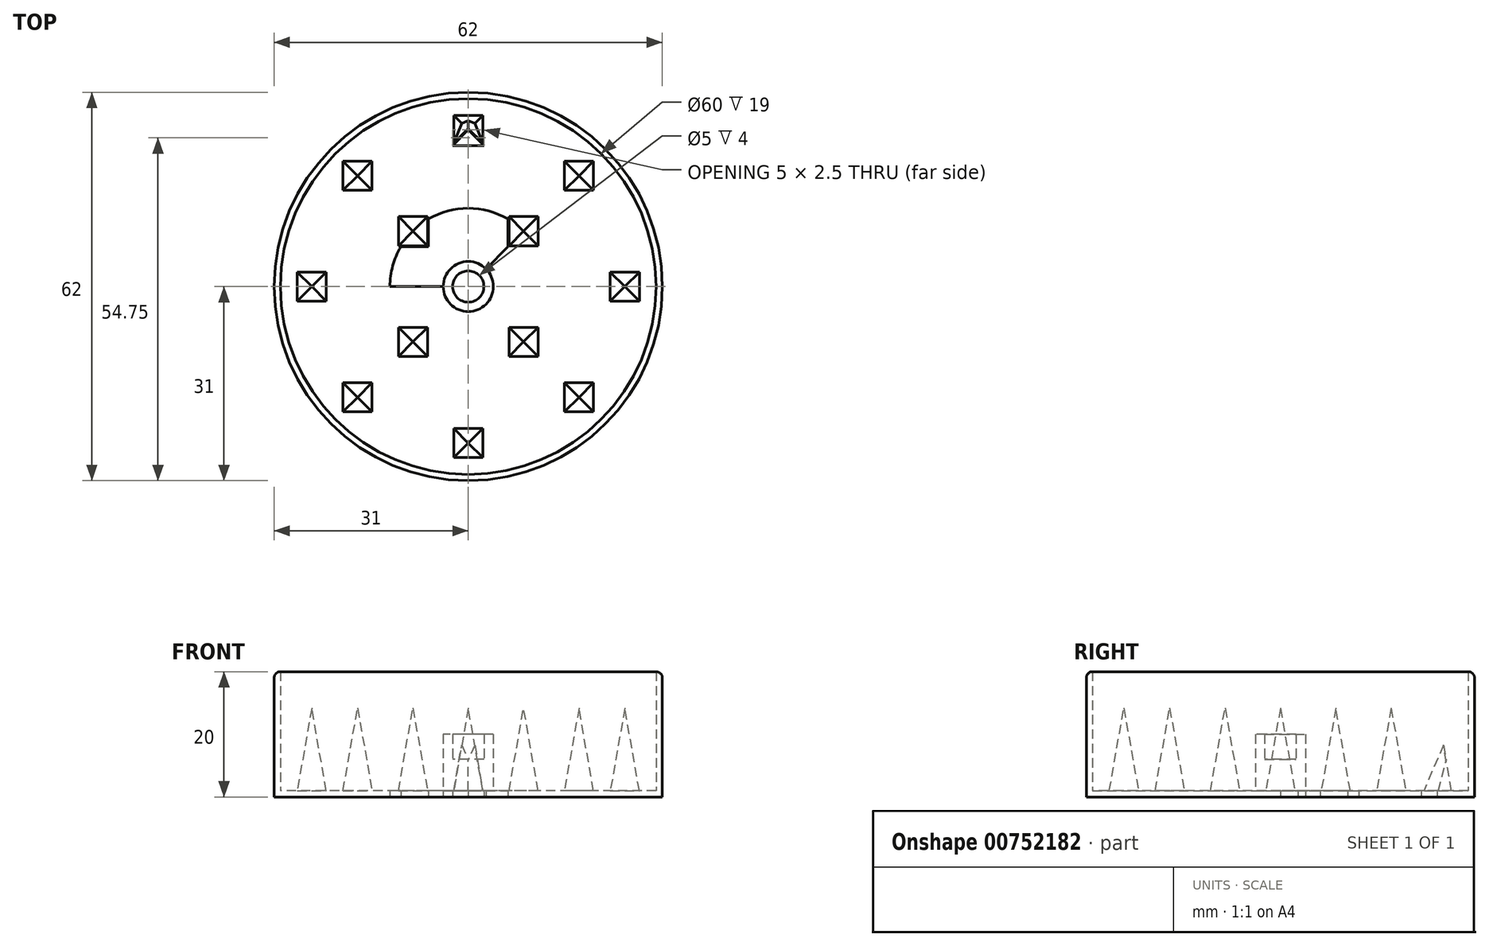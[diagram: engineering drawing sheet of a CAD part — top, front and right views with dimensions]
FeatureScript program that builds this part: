
annotation { "Feature Type Name" : "Feature", "Feature Type Description" : "" }
export const myFeature = defineFeature(function(context is Context, id is Id, definition is map)
    precondition{}
    {
        {
            var Q0;
            Q0=qCreatedBy(makeId("Top.planeOp"),FACE);
            var sketch = newSketch(context, id + "F0", { "sketchPlane" : qUnion([Q0])});
            skCircle(sketch, "E0", {"center": v(0, 0) * mm, "radius": 30 * mm});
            skCircle(sketch, "E1", {"center": v(0, 0) * mm, "radius": 31 * mm});
            skLineSegment(sketch, "E2", {"start": v(0, 0) * mm, "end": v(0, 25) * mm});
            skLineSegment(sketch, "E3", {"start": v(0, 25) * mm, "end": v(0, 0) * mm});
            skLineSegment(sketch, "E4", {"start": v(0, -25) * mm, "end": v(0, 0) * mm});
            skLineSegment(sketch, "E5", {"start": v(0, 0) * mm, "end": v(25, 0) * mm});
            skLineSegment(sketch, "E6", {"start": v(0, 0) * mm, "end": v(-25, 0) * mm});
            skLineSegment(sketch, "E7.bottom", {"start": v(-22.5, -2.5) * mm, "end": v(-27.5, -2.5) * mm});
            skLineSegment(sketch, "E7.top", {"start": v(-22.5, 2.5) * mm, "end": v(-27.5, 2.5) * mm});
            skLineSegment(sketch, "E7.left", {"start": v(-22.5, -2.5) * mm, "end": v(-22.5, 2.5) * mm});
            skLineSegment(sketch, "E7.right", {"start": v(-27.5, -2.5) * mm, "end": v(-27.5, 2.5) * mm});
            skPoint(sketch, "E7.middle", {"position": v(-25, 0) * mm});
            skLineSegment(sketch, "E8.bottom", {"start": v(2.5, 22.5) * mm, "end": v(-2.5, 22.5) * mm});
            skLineSegment(sketch, "E8.top", {"start": v(2.5, 27.5) * mm, "end": v(-2.5, 27.5) * mm});
            skLineSegment(sketch, "E8.left", {"start": v(2.5, 22.5) * mm, "end": v(2.5, 27.5) * mm});
            skLineSegment(sketch, "E8.right", {"start": v(-2.5, 22.5) * mm, "end": v(-2.5, 27.5) * mm});
            skPoint(sketch, "E8.middle", {"position": v(0, 25) * mm});
            skLineSegment(sketch, "E9.bottom", {"start": v(27.5, -2.5) * mm, "end": v(22.5, -2.5) * mm});
            skLineSegment(sketch, "E9.top", {"start": v(27.5, 2.5) * mm, "end": v(22.5, 2.5) * mm});
            skLineSegment(sketch, "E9.left", {"start": v(27.5, -2.5) * mm, "end": v(27.5, 2.5) * mm});
            skLineSegment(sketch, "E9.right", {"start": v(22.5, -2.5) * mm, "end": v(22.5, 2.5) * mm});
            skPoint(sketch, "E9.middle", {"position": v(25, 0) * mm});
            skLineSegment(sketch, "E10.bottom", {"start": v(2.5, -22.5) * mm, "end": v(-2.5, -22.5) * mm});
            skLineSegment(sketch, "E10.top", {"start": v(2.5, -27.5) * mm, "end": v(-2.5, -27.5) * mm});
            skLineSegment(sketch, "E10.left", {"start": v(2.5, -22.5) * mm, "end": v(2.5, -27.5) * mm});
            skLineSegment(sketch, "E10.right", {"start": v(-2.5, -22.5) * mm, "end": v(-2.5, -27.5) * mm});
            skPoint(sketch, "E10.middle", {"position": v(0, -25) * mm});
            skLineSegment(sketch, "E11", {"start": v(0, 0) * mm, "end": v(17.68, 17.68) * mm});
            skLineSegment(sketch, "E12.bottom", {"start": v(20.18, 15.18) * mm, "end": v(15.18, 15.18) * mm});
            skLineSegment(sketch, "E12.top", {"start": v(20.18, 20.18) * mm, "end": v(15.18, 20.18) * mm});
            skLineSegment(sketch, "E12.left", {"start": v(20.18, 15.18) * mm, "end": v(20.18, 20.18) * mm});
            skLineSegment(sketch, "E12.right", {"start": v(15.18, 15.18) * mm, "end": v(15.18, 20.18) * mm});
            skPoint(sketch, "E12.middle", {"position": v(17.68, 17.68) * mm});
            skLineSegment(sketch, "E13.1.0", {"start": v(-20.18, 20.18) * mm, "end": v(-20.18, 15.18) * mm});
            skLineSegment(sketch, "E13.1.1", {"start": v(-15.18, 20.18) * mm, "end": v(-20.18, 20.18) * mm});
            skLineSegment(sketch, "E13.1.2", {"start": v(-15.18, 20.18) * mm, "end": v(-15.18, 15.18) * mm});
            skLineSegment(sketch, "E13.1.3", {"start": v(-15.18, 15.18) * mm, "end": v(-20.18, 15.18) * mm});
            skLineSegment(sketch, "E13.2.0", {"start": v(-20.18, -20.18) * mm, "end": v(-15.18, -20.18) * mm});
            skLineSegment(sketch, "E13.2.1", {"start": v(-20.18, -15.18) * mm, "end": v(-20.18, -20.18) * mm});
            skLineSegment(sketch, "E13.2.2", {"start": v(-20.18, -15.18) * mm, "end": v(-15.18, -15.18) * mm});
            skLineSegment(sketch, "E13.2.3", {"start": v(-15.18, -15.18) * mm, "end": v(-15.18, -20.18) * mm});
            skLineSegment(sketch, "E13.3.0", {"start": v(20.18, -20.18) * mm, "end": v(20.18, -15.18) * mm});
            skLineSegment(sketch, "E13.3.1", {"start": v(15.18, -20.18) * mm, "end": v(20.18, -20.18) * mm});
            skLineSegment(sketch, "E13.3.2", {"start": v(15.18, -20.18) * mm, "end": v(15.18, -15.18) * mm});
            skLineSegment(sketch, "E13.3.3", {"start": v(15.18, -15.18) * mm, "end": v(20.18, -15.18) * mm});
            skPoint(sketch, "E14", {"position": v(8.84, 8.84) * mm});
            skLineSegment(sketch, "E15.bottom", {"start": v(11.34, 6.34) * mm, "end": v(6.34, 6.34) * mm});
            skLineSegment(sketch, "E15.top", {"start": v(11.34, 11.34) * mm, "end": v(6.34, 11.34) * mm});
            skLineSegment(sketch, "E15.left", {"start": v(11.34, 6.34) * mm, "end": v(11.34, 11.34) * mm});
            skLineSegment(sketch, "E15.right", {"start": v(6.34, 6.34) * mm, "end": v(6.34, 11.34) * mm});
            skLineSegment(sketch, "E16.1.0", {"start": v(-11.34, 11.34) * mm, "end": v(-11.34, 6.34) * mm});
            skLineSegment(sketch, "E16.1.1", {"start": v(-6.34, 11.34) * mm, "end": v(-11.34, 11.34) * mm});
            skLineSegment(sketch, "E16.1.2", {"start": v(-6.34, 11.34) * mm, "end": v(-6.34, 6.34) * mm});
            skLineSegment(sketch, "E16.1.3", {"start": v(-6.34, 6.34) * mm, "end": v(-11.34, 6.34) * mm});
            skLineSegment(sketch, "E16.2.0", {"start": v(-11.34, -11.34) * mm, "end": v(-6.34, -11.34) * mm});
            skLineSegment(sketch, "E16.2.1", {"start": v(-11.34, -6.34) * mm, "end": v(-11.34, -11.34) * mm});
            skLineSegment(sketch, "E16.2.2", {"start": v(-11.34, -6.34) * mm, "end": v(-6.34, -6.34) * mm});
            skLineSegment(sketch, "E16.2.3", {"start": v(-6.34, -6.34) * mm, "end": v(-6.34, -11.34) * mm});
            skLineSegment(sketch, "E16.3.0", {"start": v(11.34, -11.34) * mm, "end": v(11.34, -6.34) * mm});
            skLineSegment(sketch, "E16.3.1", {"start": v(6.34, -11.34) * mm, "end": v(11.34, -11.34) * mm});
            skLineSegment(sketch, "E16.3.2", {"start": v(6.34, -11.34) * mm, "end": v(6.34, -6.34) * mm});
            skLineSegment(sketch, "E16.3.3", {"start": v(6.34, -6.34) * mm, "end": v(11.34, -6.34) * mm});
            skCircle(sketch, "E17", {"center": v(0, 0) * mm, "radius": 4 * mm});
            skLineSegment(sketch, "E18", {"start": v(-20.18, 20.18) * mm, "end": v(-15.18, 15.18) * mm});
            skLineSegment(sketch, "E19", {"start": v(-2.5, 27.5) * mm, "end": v(2.5, 22.5) * mm});
            skLineSegment(sketch, "E20", {"start": v(15.18, 20.18) * mm, "end": v(20.18, 15.18) * mm});
            skLineSegment(sketch, "E21", {"start": v(22.5, 2.5) * mm, "end": v(27.5, -2.5) * mm});
            skLineSegment(sketch, "E22", {"start": v(-11.34, 11.34) * mm, "end": v(-6.34, 6.34) * mm});
            skLineSegment(sketch, "E23", {"start": v(6.34, -6.34) * mm, "end": v(11.34, -11.34) * mm});
            skLineSegment(sketch, "E24", {"start": v(15.18, -15.18) * mm, "end": v(20.18, -20.18) * mm});
            skLineSegment(sketch, "E25", {"start": v(-11.34, -6.34) * mm, "end": v(-6.34, -11.34) * mm});
            skLineSegment(sketch, "E26", {"start": v(-2.5, -22.5) * mm, "end": v(2.5, -27.5) * mm});
            skLineSegment(sketch, "E27", {"start": v(-20.18, -15.18) * mm, "end": v(-15.18, -20.18) * mm});
            skLineSegment(sketch, "E28", {"start": v(2.5, 27.5) * mm, "end": v(-2.5, 22.5) * mm});
            skLineSegment(sketch, "E29", {"start": v(-15.18, 20.18) * mm, "end": v(-20.18, 15.18) * mm});
            skLineSegment(sketch, "E30", {"start": v(-22.5, 2.5) * mm, "end": v(-27.5, -2.5) * mm});
            skLineSegment(sketch, "E31", {"start": v(-27.5, 2.5) * mm, "end": v(-22.5, -2.5) * mm});
            skLineSegment(sketch, "E32", {"start": v(-6.34, 11.34) * mm, "end": v(-11.34, 6.34) * mm});
            skLineSegment(sketch, "E33", {"start": v(6.34, 11.34) * mm, "end": v(11.34, 6.34) * mm});
            skLineSegment(sketch, "E34", {"start": v(20.18, 20.18) * mm, "end": v(17.68, 17.68) * mm});
            skLineSegment(sketch, "E35", {"start": v(27.5, 2.5) * mm, "end": v(22.5, -2.5) * mm});
            skLineSegment(sketch, "E36", {"start": v(20.18, -15.18) * mm, "end": v(15.18, -20.18) * mm});
            skLineSegment(sketch, "E37", {"start": v(11.34, -6.34) * mm, "end": v(6.34, -11.34) * mm});
            skLineSegment(sketch, "E38", {"start": v(-6.34, -6.34) * mm, "end": v(-11.34, -11.34) * mm});
            skLineSegment(sketch, "E39", {"start": v(-15.18, -15.18) * mm, "end": v(-20.18, -20.18) * mm});
            skLineSegment(sketch, "E40", {"start": v(2.5, -22.5) * mm, "end": v(-2.5, -27.5) * mm});
            skCircle(sketch, "E41", {"center": v(0, 0) * mm, "radius": 12.5 * mm});
            skCircle(sketch, "E42", {"center": v(0, 0) * mm, "radius": 21.46 * mm});
            skCircle(sketch, "E43", {"center": v(0, 0) * mm, "radius": 2.5 * mm});
            skSolve(sketch);
        }
        {
            var Q0;
            Q0 = qSketchRegion(id + "F0", true);
            var Q1;
            Q1=makeQuery(id+"F0.imprint","IMPRINT",FACE,{"disambiguationData":[TD([[makeQuery(id+"F0.imprint","IMPRINT",EDGE,{"derivedFrom":sQuery(id+"F0.wireOp",EDGE,"E0")}),1.0]])]});
            var Q2;
            {var subQ1=sQuery(id+"F0.wireOp",EDGE,"E15.top");Q2=makeQuery(id+"F0.imprint","IMPRINT",FACE,{"disambiguationData":[TD([[makeQuery(id+"F0.imprint","IMPRINT",EDGE,{"derivedFrom":subQ1}),-1.0]])]});}
            var Q3;
            {var subQ0=sQuery(id+"F0.wireOp",EDGE,"E15.left");Q3=makeQuery(id+"F0.imprint","IMPRINT",FACE,{"disambiguationData":[TD([[makeQuery(id+"F0.imprint","IMPRINT",EDGE,{"derivedFrom":subQ0}),-1.0]])]});}
            var Q4;
            {var subQ5=sQuery(id+"F0.wireOp",EDGE,"E16.3.0");Q4=makeQuery(id+"F0.imprint","IMPRINT",FACE,{"disambiguationData":[TD([[makeQuery(id+"F0.imprint","IMPRINT",EDGE,{"derivedFrom":subQ5}),-1.0]])]});}
            var Q5;
            {var subQ9=sQuery(id+"F0.wireOp",EDGE,"E16.2.0");Q5=makeQuery(id+"F0.imprint","IMPRINT",FACE,{"disambiguationData":[TD([[makeQuery(id+"F0.imprint","IMPRINT",EDGE,{"derivedFrom":subQ9}),-1.0]])]});}
            var Q6;
            {var subQ1=sQuery(id+"F0.wireOp",EDGE,"E16.1.0");Q6=makeQuery(id+"F0.imprint","IMPRINT",FACE,{"disambiguationData":[TD([[makeQuery(id+"F0.imprint","IMPRINT",EDGE,{"derivedFrom":subQ1}),-1.0]])]});}
            var Q7;
            {var subQ3=sQuery(id+"F0.wireOp",EDGE,"E41");var subQ9=sQuery(id+"F0.wireOp",EDGE,"E3");var subQ10=makeQuery(id+"F0.imprint","INTERSECT",VERTEX,{"derivedFrom":[subQ9,subQ3]});Q7=makeQuery(id+"F0.imprint","IMPRINT",FACE,{"disambiguationData":[TD([[makeQuery(id+"F0.imprint","IMPRINT",EDGE,{"disambiguationData":[TD([[subQ10,-1.0]])],"derivedFrom":subQ9}),-1.0]])]});}
            var Q8;
            {var subQ1=sQuery(id+"F0.wireOp",EDGE,"E3");var subQ7=sQuery(id+"F0.wireOp",EDGE,"E41");var subQ9=makeQuery(id+"F0.imprint","INTERSECT",VERTEX,{"derivedFrom":[subQ1,subQ7]});Q8=makeQuery(id+"F0.imprint","IMPRINT",FACE,{"disambiguationData":[TD([[makeQuery(id+"F0.imprint","IMPRINT",EDGE,{"disambiguationData":[TD([[subQ9,-1.0]])],"derivedFrom":subQ1}),1.0]])]});}
            var Q9;
            {var subQ0=sQuery(id+"F0.wireOp",EDGE,"E17");var subQ1=sQuery(id+"F0.wireOp",EDGE,"E5");var subQ2=makeQuery(id+"F0.imprint","INTERSECT",VERTEX,{"derivedFrom":[subQ1,subQ0]});Q9=makeQuery(id+"F0.imprint","IMPRINT",FACE,{"disambiguationData":[TD([[makeQuery(id+"F0.imprint","IMPRINT",EDGE,{"disambiguationData":[TD([[subQ2,-1.0]])],"derivedFrom":subQ1}),1.0]])]});}
            var Q10;
            {var subQ3=sQuery(id+"F0.wireOp",EDGE,"E41");var subQ10=sQuery(id+"F0.wireOp",EDGE,"E4");var subQ12=makeQuery(id+"F0.imprint","INTERSECT",VERTEX,{"derivedFrom":[subQ10,subQ3]});Q10=makeQuery(id+"F0.imprint","IMPRINT",FACE,{"disambiguationData":[TD([[makeQuery(id+"F0.imprint","IMPRINT",EDGE,{"disambiguationData":[TD([[subQ12,-1.0]])],"derivedFrom":subQ10}),-1.0]])]});}
            var Q11;
            {var subQ3=sQuery(id+"F0.wireOp",EDGE,"E41");var subQ6=sQuery(id+"F0.wireOp",EDGE,"E4");var subQ12=makeQuery(id+"F0.imprint","INTERSECT",VERTEX,{"derivedFrom":[subQ6,subQ3]});Q11=makeQuery(id+"F0.imprint","IMPRINT",FACE,{"disambiguationData":[TD([[makeQuery(id+"F0.imprint","IMPRINT",EDGE,{"disambiguationData":[TD([[subQ12,-1.0]])],"derivedFrom":subQ6}),1.0]])]});}
            var Q12;
            {var subQ0=sQuery(id+"F0.wireOp",EDGE,"E9.top");Q12=makeQuery(id+"F0.imprint","IMPRINT",FACE,{"disambiguationData":[TD([[makeQuery(id+"F0.imprint","IMPRINT",EDGE,{"derivedFrom":subQ0}),1.0]])]});}
            var Q13;
            {var subQ0=sQuery(id+"F0.wireOp",EDGE,"E9.left");Q13=makeQuery(id+"F0.imprint","IMPRINT",FACE,{"disambiguationData":[TD([[makeQuery(id+"F0.imprint","IMPRINT",EDGE,{"derivedFrom":subQ0}),1.0]])]});}
            var Q14;
            {var subQ0=sQuery(id+"F0.wireOp",EDGE,"E9.bottom");Q14=makeQuery(id+"F0.imprint","IMPRINT",FACE,{"disambiguationData":[TD([[makeQuery(id+"F0.imprint","IMPRINT",EDGE,{"derivedFrom":subQ0}),-1.0]])]});}
            var Q15;
            {var subQ1=sQuery(id+"F0.wireOp",EDGE,"E5");var subQ3=sQuery(id+"F0.wireOp",EDGE,"E9.right");var subQ4=makeQuery(id+"F0.imprint","INTERSECT",VERTEX,{"derivedFrom":[subQ1,subQ3]});Q15=makeQuery(id+"F0.imprint","IMPRINT",FACE,{"disambiguationData":[TD([[makeQuery(id+"F0.imprint","IMPRINT",EDGE,{"disambiguationData":[TD([[subQ4,-1.0]])],"derivedFrom":subQ1}),-1.0]])]});}
            var Q16;
            {var subQ1=sQuery(id+"F0.wireOp",EDGE,"E5");var subQ3=sQuery(id+"F0.wireOp",EDGE,"E9.right");var subQ4=makeQuery(id+"F0.imprint","INTERSECT",VERTEX,{"derivedFrom":[subQ1,subQ3]});Q16=makeQuery(id+"F0.imprint","IMPRINT",FACE,{"disambiguationData":[TD([[makeQuery(id+"F0.imprint","IMPRINT",EDGE,{"disambiguationData":[TD([[subQ4,-1.0]])],"derivedFrom":subQ1}),1.0]])]});}
            var Q17;
            {var subQ3=sQuery(id+"F0.wireOp",EDGE,"E12.bottom");Q17=makeQuery(id+"F0.imprint","IMPRINT",FACE,{"disambiguationData":[TD([[makeQuery(id+"F0.imprint","IMPRINT",EDGE,{"derivedFrom":subQ3}),-1.0]])]});}
            var Q18;
            {var subQ0=sQuery(id+"F0.wireOp",EDGE,"E12.top");Q18=makeQuery(id+"F0.imprint","IMPRINT",FACE,{"disambiguationData":[TD([[makeQuery(id+"F0.imprint","IMPRINT",EDGE,{"derivedFrom":subQ0}),1.0]])]});}
            var Q19;
            {var subQ0=sQuery(id+"F0.wireOp",EDGE,"E12.left");Q19=makeQuery(id+"F0.imprint","IMPRINT",FACE,{"disambiguationData":[TD([[makeQuery(id+"F0.imprint","IMPRINT",EDGE,{"derivedFrom":subQ0}),1.0]])]});}
            var Q20;
            {var subQ3=sQuery(id+"F0.wireOp",EDGE,"E12.right");Q20=makeQuery(id+"F0.imprint","IMPRINT",FACE,{"disambiguationData":[TD([[makeQuery(id+"F0.imprint","IMPRINT",EDGE,{"derivedFrom":subQ3}),-1.0]])]});}
            var Q21;
            {var subQ0=sQuery(id+"F0.wireOp",EDGE,"E8.top");Q21=makeQuery(id+"F0.imprint","IMPRINT",FACE,{"disambiguationData":[TD([[makeQuery(id+"F0.imprint","IMPRINT",EDGE,{"derivedFrom":subQ0}),1.0]])]});}
            var Q22;
            {var subQ0=sQuery(id+"F0.wireOp",EDGE,"E8.left");Q22=makeQuery(id+"F0.imprint","IMPRINT",FACE,{"disambiguationData":[TD([[makeQuery(id+"F0.imprint","IMPRINT",EDGE,{"derivedFrom":subQ0}),1.0]])]});}
            var Q23;
            {var subQ1=sQuery(id+"F0.wireOp",EDGE,"E3");var subQ3=sQuery(id+"F0.wireOp",EDGE,"E8.bottom");var subQ4=makeQuery(id+"F0.imprint","INTERSECT",VERTEX,{"derivedFrom":[subQ1,subQ3]});Q23=makeQuery(id+"F0.imprint","IMPRINT",FACE,{"disambiguationData":[TD([[makeQuery(id+"F0.imprint","IMPRINT",EDGE,{"disambiguationData":[TD([[subQ4,1.0]])],"derivedFrom":subQ1}),1.0]])]});}
            var Q24;
            {var subQ1=sQuery(id+"F0.wireOp",EDGE,"E3");var subQ3=sQuery(id+"F0.wireOp",EDGE,"E8.bottom");var subQ4=makeQuery(id+"F0.imprint","INTERSECT",VERTEX,{"derivedFrom":[subQ1,subQ3]});Q24=makeQuery(id+"F0.imprint","IMPRINT",FACE,{"disambiguationData":[TD([[makeQuery(id+"F0.imprint","IMPRINT",EDGE,{"disambiguationData":[TD([[subQ4,1.0]])],"derivedFrom":subQ1}),-1.0]])]});}
            var Q25;
            {var subQ0=sQuery(id+"F0.wireOp",EDGE,"E8.right");Q25=makeQuery(id+"F0.imprint","IMPRINT",FACE,{"disambiguationData":[TD([[makeQuery(id+"F0.imprint","IMPRINT",EDGE,{"derivedFrom":subQ0}),-1.0]])]});}
            var Q26;
            {var subQ0=sQuery(id+"F0.wireOp",EDGE,"E13.1.1");Q26=makeQuery(id+"F0.imprint","IMPRINT",FACE,{"disambiguationData":[TD([[makeQuery(id+"F0.imprint","IMPRINT",EDGE,{"derivedFrom":subQ0}),1.0]])]});}
            var Q27;
            {var subQ0=sQuery(id+"F0.wireOp",EDGE,"E13.1.2");Q27=makeQuery(id+"F0.imprint","IMPRINT",FACE,{"disambiguationData":[TD([[makeQuery(id+"F0.imprint","IMPRINT",EDGE,{"derivedFrom":subQ0}),-1.0]])]});}
            var Q28;
            {var subQ0=sQuery(id+"F0.wireOp",EDGE,"E13.1.3");Q28=makeQuery(id+"F0.imprint","IMPRINT",FACE,{"disambiguationData":[TD([[makeQuery(id+"F0.imprint","IMPRINT",EDGE,{"derivedFrom":subQ0}),-1.0]])]});}
            var Q29;
            {var subQ0=sQuery(id+"F0.wireOp",EDGE,"E13.1.0");Q29=makeQuery(id+"F0.imprint","IMPRINT",FACE,{"disambiguationData":[TD([[makeQuery(id+"F0.imprint","IMPRINT",EDGE,{"derivedFrom":subQ0}),1.0]])]});}
            var Q30;
            {var subQ0=sQuery(id+"F0.wireOp",EDGE,"E16.1.1");Q30=makeQuery(id+"F0.imprint","IMPRINT",FACE,{"disambiguationData":[TD([[makeQuery(id+"F0.imprint","IMPRINT",EDGE,{"derivedFrom":subQ0}),1.0]])]});}
            var Q31;
            {var subQ0=sQuery(id+"F0.wireOp",EDGE,"E16.1.0");Q31=makeQuery(id+"F0.imprint","IMPRINT",FACE,{"disambiguationData":[TD([[makeQuery(id+"F0.imprint","IMPRINT",EDGE,{"derivedFrom":subQ0}),1.0]])]});}
            var Q32;
            {var subQ1=sQuery(id+"F0.wireOp",EDGE,"E16.1.3");var subQ3=sQuery(id+"F0.wireOp",EDGE,"E41");var subQ4=makeQuery(id+"F0.imprint","INTERSECT",VERTEX,{"derivedFrom":[subQ1,subQ3]});Q32=makeQuery(id+"F0.imprint","IMPRINT",FACE,{"disambiguationData":[TD([[makeQuery(id+"F0.imprint","IMPRINT",EDGE,{"disambiguationData":[TD([[subQ4,1.0]])],"derivedFrom":subQ1}),-1.0]])]});}
            var Q33;
            {var subQ1=sQuery(id+"F0.wireOp",EDGE,"E16.1.2");var subQ3=sQuery(id+"F0.wireOp",EDGE,"E41");var subQ4=makeQuery(id+"F0.imprint","INTERSECT",VERTEX,{"derivedFrom":[subQ1,subQ3]});Q33=makeQuery(id+"F0.imprint","IMPRINT",FACE,{"disambiguationData":[TD([[makeQuery(id+"F0.imprint","IMPRINT",EDGE,{"disambiguationData":[TD([[subQ4,-1.0]])],"derivedFrom":subQ1}),-1.0]])]});}
            var Q34;
            {var subQ0=sQuery(id+"F0.wireOp",EDGE,"E15.right");var subQ3=sQuery(id+"F0.wireOp",EDGE,"E41");var subQ5=makeQuery(id+"F0.imprint","INTERSECT",VERTEX,{"derivedFrom":[subQ0,subQ3]});Q34=makeQuery(id+"F0.imprint","IMPRINT",FACE,{"disambiguationData":[TD([[makeQuery(id+"F0.imprint","IMPRINT",EDGE,{"disambiguationData":[TD([[subQ5,1.0]])],"derivedFrom":subQ0}),-1.0]])]});}
            var Q35;
            {var subQ0=sQuery(id+"F0.wireOp",EDGE,"E15.top");Q35=makeQuery(id+"F0.imprint","IMPRINT",FACE,{"disambiguationData":[TD([[makeQuery(id+"F0.imprint","IMPRINT",EDGE,{"derivedFrom":subQ0}),1.0]])]});}
            var Q36;
            {var subQ0=sQuery(id+"F0.wireOp",EDGE,"E15.left");Q36=makeQuery(id+"F0.imprint","IMPRINT",FACE,{"disambiguationData":[TD([[makeQuery(id+"F0.imprint","IMPRINT",EDGE,{"derivedFrom":subQ0}),1.0]])]});}
            var Q37;
            {var subQ0=sQuery(id+"F0.wireOp",EDGE,"E15.bottom");var subQ3=sQuery(id+"F0.wireOp",EDGE,"E41");var subQ5=makeQuery(id+"F0.imprint","INTERSECT",VERTEX,{"derivedFrom":[subQ0,subQ3]});Q37=makeQuery(id+"F0.imprint","IMPRINT",FACE,{"disambiguationData":[TD([[makeQuery(id+"F0.imprint","IMPRINT",EDGE,{"disambiguationData":[TD([[subQ5,-1.0]])],"derivedFrom":subQ0}),-1.0]])]});}
            var Q38;
            {var subQ1=sQuery(id+"F0.wireOp",EDGE,"E16.3.3");var subQ3=sQuery(id+"F0.wireOp",EDGE,"E41");var subQ4=makeQuery(id+"F0.imprint","INTERSECT",VERTEX,{"derivedFrom":[subQ1,subQ3]});Q38=makeQuery(id+"F0.imprint","IMPRINT",FACE,{"disambiguationData":[TD([[makeQuery(id+"F0.imprint","IMPRINT",EDGE,{"disambiguationData":[TD([[subQ4,1.0]])],"derivedFrom":subQ1}),-1.0]])]});}
            var Q39;
            {var subQ0=sQuery(id+"F0.wireOp",EDGE,"E16.3.0");Q39=makeQuery(id+"F0.imprint","IMPRINT",FACE,{"disambiguationData":[TD([[makeQuery(id+"F0.imprint","IMPRINT",EDGE,{"derivedFrom":subQ0}),1.0]])]});}
            var Q40;
            {var subQ0=sQuery(id+"F0.wireOp",EDGE,"E16.3.1");Q40=makeQuery(id+"F0.imprint","IMPRINT",FACE,{"disambiguationData":[TD([[makeQuery(id+"F0.imprint","IMPRINT",EDGE,{"derivedFrom":subQ0}),1.0]])]});}
            var Q41;
            {var subQ1=sQuery(id+"F0.wireOp",EDGE,"E16.3.2");var subQ3=sQuery(id+"F0.wireOp",EDGE,"E41");var subQ4=makeQuery(id+"F0.imprint","INTERSECT",VERTEX,{"derivedFrom":[subQ1,subQ3]});Q41=makeQuery(id+"F0.imprint","IMPRINT",FACE,{"disambiguationData":[TD([[makeQuery(id+"F0.imprint","IMPRINT",EDGE,{"disambiguationData":[TD([[subQ4,-1.0]])],"derivedFrom":subQ1}),-1.0]])]});}
            var Q42;
            {var subQ1=sQuery(id+"F0.wireOp",EDGE,"E16.2.2");var subQ3=sQuery(id+"F0.wireOp",EDGE,"E41");var subQ4=makeQuery(id+"F0.imprint","INTERSECT",VERTEX,{"derivedFrom":[subQ1,subQ3]});Q42=makeQuery(id+"F0.imprint","IMPRINT",FACE,{"disambiguationData":[TD([[makeQuery(id+"F0.imprint","IMPRINT",EDGE,{"disambiguationData":[TD([[subQ4,-1.0]])],"derivedFrom":subQ1}),-1.0]])]});}
            var Q43;
            {var subQ1=sQuery(id+"F0.wireOp",EDGE,"E16.2.3");var subQ3=sQuery(id+"F0.wireOp",EDGE,"E41");var subQ4=makeQuery(id+"F0.imprint","INTERSECT",VERTEX,{"derivedFrom":[subQ1,subQ3]});Q43=makeQuery(id+"F0.imprint","IMPRINT",FACE,{"disambiguationData":[TD([[makeQuery(id+"F0.imprint","IMPRINT",EDGE,{"disambiguationData":[TD([[subQ4,1.0]])],"derivedFrom":subQ1}),-1.0]])]});}
            var Q44;
            {var subQ0=sQuery(id+"F0.wireOp",EDGE,"E16.2.0");Q44=makeQuery(id+"F0.imprint","IMPRINT",FACE,{"disambiguationData":[TD([[makeQuery(id+"F0.imprint","IMPRINT",EDGE,{"derivedFrom":subQ0}),1.0]])]});}
            var Q45;
            {var subQ0=sQuery(id+"F0.wireOp",EDGE,"E7.top");Q45=makeQuery(id+"F0.imprint","IMPRINT",FACE,{"disambiguationData":[TD([[makeQuery(id+"F0.imprint","IMPRINT",EDGE,{"derivedFrom":subQ0}),1.0]])]});}
            var Q46;
            {var subQ1=sQuery(id+"F0.wireOp",EDGE,"E6");var subQ3=sQuery(id+"F0.wireOp",EDGE,"E7.left");var subQ4=makeQuery(id+"F0.imprint","INTERSECT",VERTEX,{"derivedFrom":[subQ1,subQ3]});Q46=makeQuery(id+"F0.imprint","IMPRINT",FACE,{"disambiguationData":[TD([[makeQuery(id+"F0.imprint","IMPRINT",EDGE,{"disambiguationData":[TD([[subQ4,-1.0]])],"derivedFrom":subQ1}),-1.0]])]});}
            var Q47;
            {var subQ1=sQuery(id+"F0.wireOp",EDGE,"E6");var subQ3=sQuery(id+"F0.wireOp",EDGE,"E7.left");var subQ4=makeQuery(id+"F0.imprint","INTERSECT",VERTEX,{"derivedFrom":[subQ1,subQ3]});Q47=makeQuery(id+"F0.imprint","IMPRINT",FACE,{"disambiguationData":[TD([[makeQuery(id+"F0.imprint","IMPRINT",EDGE,{"disambiguationData":[TD([[subQ4,-1.0]])],"derivedFrom":subQ1}),1.0]])]});}
            var Q48;
            {var subQ0=sQuery(id+"F0.wireOp",EDGE,"E7.bottom");Q48=makeQuery(id+"F0.imprint","IMPRINT",FACE,{"disambiguationData":[TD([[makeQuery(id+"F0.imprint","IMPRINT",EDGE,{"derivedFrom":subQ0}),-1.0]])]});}
            var Q49;
            {var subQ0=sQuery(id+"F0.wireOp",EDGE,"E7.right");Q49=makeQuery(id+"F0.imprint","IMPRINT",FACE,{"disambiguationData":[TD([[makeQuery(id+"F0.imprint","IMPRINT",EDGE,{"derivedFrom":subQ0}),-1.0]])]});}
            var Q50;
            {var subQ1=sQuery(id+"F0.wireOp",EDGE,"E3");var subQ3=sQuery(id+"F0.wireOp",EDGE,"E17");var subQ4=makeQuery(id+"F0.imprint","INTERSECT",VERTEX,{"derivedFrom":[subQ1,subQ3]});Q50=makeQuery(id+"F0.imprint","IMPRINT",FACE,{"disambiguationData":[TD([[makeQuery(id+"F0.imprint","IMPRINT",EDGE,{"disambiguationData":[TD([[subQ4,-1.0]])],"derivedFrom":subQ3}),1.0]])]});}
            var Q51;
            {var subQ1=sQuery(id+"F0.wireOp",EDGE,"E4");var subQ3=sQuery(id+"F0.wireOp",EDGE,"E17");var subQ4=makeQuery(id+"F0.imprint","INTERSECT",VERTEX,{"derivedFrom":[subQ1,subQ3]});Q51=makeQuery(id+"F0.imprint","IMPRINT",FACE,{"disambiguationData":[TD([[makeQuery(id+"F0.imprint","IMPRINT",EDGE,{"disambiguationData":[TD([[subQ4,-1.0]])],"derivedFrom":subQ3}),1.0]])]});}
            var Q52;
            {var subQ1=sQuery(id+"F0.wireOp",EDGE,"E4");var subQ3=sQuery(id+"F0.wireOp",EDGE,"E17");var subQ4=makeQuery(id+"F0.imprint","INTERSECT",VERTEX,{"derivedFrom":[subQ1,subQ3]});Q52=makeQuery(id+"F0.imprint","IMPRINT",FACE,{"disambiguationData":[TD([[makeQuery(id+"F0.imprint","IMPRINT",EDGE,{"disambiguationData":[TD([[subQ4,1.0]])],"derivedFrom":subQ3}),1.0]])]});}
            var Q53;
            {var subQ1=sQuery(id+"F0.wireOp",EDGE,"E5");var subQ3=sQuery(id+"F0.wireOp",EDGE,"E17");var subQ4=makeQuery(id+"F0.imprint","INTERSECT",VERTEX,{"derivedFrom":[subQ1,subQ3]});Q53=makeQuery(id+"F0.imprint","IMPRINT",FACE,{"disambiguationData":[TD([[makeQuery(id+"F0.imprint","IMPRINT",EDGE,{"disambiguationData":[TD([[subQ4,-1.0]])],"derivedFrom":subQ3}),1.0]])]});}
            var Q54;
            {var subQ1=sQuery(id+"F0.wireOp",EDGE,"E3");var subQ3=sQuery(id+"F0.wireOp",EDGE,"E17");var subQ4=makeQuery(id+"F0.imprint","INTERSECT",VERTEX,{"derivedFrom":[subQ1,subQ3]});Q54=makeQuery(id+"F0.imprint","IMPRINT",FACE,{"disambiguationData":[TD([[makeQuery(id+"F0.imprint","IMPRINT",EDGE,{"disambiguationData":[TD([[subQ4,1.0]])],"derivedFrom":subQ3}),1.0]])]});}
            var Q55;
            {var subQ0=sQuery(id+"F0.wireOp",EDGE,"E16.2.1");Q55=makeQuery(id+"F0.imprint","IMPRINT",FACE,{"disambiguationData":[TD([[makeQuery(id+"F0.imprint","IMPRINT",EDGE,{"derivedFrom":subQ0}),1.0]])]});}
            var Q56;
            {var subQ0=sQuery(id+"F0.wireOp",EDGE,"E13.2.2");Q56=makeQuery(id+"F0.imprint","IMPRINT",FACE,{"disambiguationData":[TD([[makeQuery(id+"F0.imprint","IMPRINT",EDGE,{"derivedFrom":subQ0}),-1.0]])]});}
            var Q57;
            {var subQ0=sQuery(id+"F0.wireOp",EDGE,"E13.2.3");Q57=makeQuery(id+"F0.imprint","IMPRINT",FACE,{"disambiguationData":[TD([[makeQuery(id+"F0.imprint","IMPRINT",EDGE,{"derivedFrom":subQ0}),-1.0]])]});}
            var Q58;
            {var subQ0=sQuery(id+"F0.wireOp",EDGE,"E13.2.0");Q58=makeQuery(id+"F0.imprint","IMPRINT",FACE,{"disambiguationData":[TD([[makeQuery(id+"F0.imprint","IMPRINT",EDGE,{"derivedFrom":subQ0}),1.0]])]});}
            var Q59;
            {var subQ0=sQuery(id+"F0.wireOp",EDGE,"E13.2.1");Q59=makeQuery(id+"F0.imprint","IMPRINT",FACE,{"disambiguationData":[TD([[makeQuery(id+"F0.imprint","IMPRINT",EDGE,{"derivedFrom":subQ0}),1.0]])]});}
            var Q60;
            {var subQ0=sQuery(id+"F0.wireOp",EDGE,"E13.3.3");Q60=makeQuery(id+"F0.imprint","IMPRINT",FACE,{"disambiguationData":[TD([[makeQuery(id+"F0.imprint","IMPRINT",EDGE,{"derivedFrom":subQ0}),-1.0]])]});}
            var Q61;
            {var subQ0=sQuery(id+"F0.wireOp",EDGE,"E13.3.0");Q61=makeQuery(id+"F0.imprint","IMPRINT",FACE,{"disambiguationData":[TD([[makeQuery(id+"F0.imprint","IMPRINT",EDGE,{"derivedFrom":subQ0}),1.0]])]});}
            var Q62;
            {var subQ0=sQuery(id+"F0.wireOp",EDGE,"E13.3.1");Q62=makeQuery(id+"F0.imprint","IMPRINT",FACE,{"disambiguationData":[TD([[makeQuery(id+"F0.imprint","IMPRINT",EDGE,{"derivedFrom":subQ0}),1.0]])]});}
            var Q63;
            {var subQ0=sQuery(id+"F0.wireOp",EDGE,"E13.3.2");Q63=makeQuery(id+"F0.imprint","IMPRINT",FACE,{"disambiguationData":[TD([[makeQuery(id+"F0.imprint","IMPRINT",EDGE,{"derivedFrom":subQ0}),-1.0]])]});}
            var Q64;
            {var subQ0=sQuery(id+"F0.wireOp",EDGE,"E10.left");Q64=makeQuery(id+"F0.imprint","IMPRINT",FACE,{"disambiguationData":[TD([[makeQuery(id+"F0.imprint","IMPRINT",EDGE,{"derivedFrom":subQ0}),-1.0]])]});}
            var Q65;
            {var subQ0=sQuery(id+"F0.wireOp",EDGE,"E10.top");Q65=makeQuery(id+"F0.imprint","IMPRINT",FACE,{"disambiguationData":[TD([[makeQuery(id+"F0.imprint","IMPRINT",EDGE,{"derivedFrom":subQ0}),-1.0]])]});}
            var Q66;
            {var subQ0=sQuery(id+"F0.wireOp",EDGE,"E10.right");Q66=makeQuery(id+"F0.imprint","IMPRINT",FACE,{"disambiguationData":[TD([[makeQuery(id+"F0.imprint","IMPRINT",EDGE,{"derivedFrom":subQ0}),1.0]])]});}
            var Q67;
            {var subQ1=sQuery(id+"F0.wireOp",EDGE,"E4");var subQ3=sQuery(id+"F0.wireOp",EDGE,"E10.bottom");var subQ4=makeQuery(id+"F0.imprint","INTERSECT",VERTEX,{"derivedFrom":[subQ1,subQ3]});Q67=makeQuery(id+"F0.imprint","IMPRINT",FACE,{"disambiguationData":[TD([[makeQuery(id+"F0.imprint","IMPRINT",EDGE,{"disambiguationData":[TD([[subQ4,1.0]])],"derivedFrom":subQ1}),1.0]])]});}
            var Q68;
            {var subQ1=sQuery(id+"F0.wireOp",EDGE,"E4");var subQ3=sQuery(id+"F0.wireOp",EDGE,"E10.bottom");var subQ4=makeQuery(id+"F0.imprint","INTERSECT",VERTEX,{"derivedFrom":[subQ1,subQ3]});Q68=makeQuery(id+"F0.imprint","IMPRINT",FACE,{"disambiguationData":[TD([[makeQuery(id+"F0.imprint","IMPRINT",EDGE,{"disambiguationData":[TD([[subQ4,1.0]])],"derivedFrom":subQ1}),-1.0]])]});}
            var Q69;
            {var subQ1=sQuery(id+"F0.wireOp",EDGE,"E16.3.3");var subQ3=sQuery(id+"F0.wireOp",EDGE,"E41");var subQ4=makeQuery(id+"F0.imprint","INTERSECT",VERTEX,{"derivedFrom":[subQ1,subQ3]});Q69=makeQuery(id+"F0.imprint","IMPRINT",FACE,{"disambiguationData":[TD([[makeQuery(id+"F0.imprint","IMPRINT",EDGE,{"disambiguationData":[TD([[subQ4,-1.0]])],"derivedFrom":subQ1}),-1.0]])]});}
            var Q70;
            {var subQ1=sQuery(id+"F0.wireOp",EDGE,"E16.3.2");var subQ3=sQuery(id+"F0.wireOp",EDGE,"E41");var subQ4=makeQuery(id+"F0.imprint","INTERSECT",VERTEX,{"derivedFrom":[subQ1,subQ3]});Q70=makeQuery(id+"F0.imprint","IMPRINT",FACE,{"disambiguationData":[TD([[makeQuery(id+"F0.imprint","IMPRINT",EDGE,{"disambiguationData":[TD([[subQ4,1.0]])],"derivedFrom":subQ1}),-1.0]])]});}
            var Q71;
            {var subQ1=sQuery(id+"F0.wireOp",EDGE,"E16.2.3");var subQ3=sQuery(id+"F0.wireOp",EDGE,"E41");var subQ4=makeQuery(id+"F0.imprint","INTERSECT",VERTEX,{"derivedFrom":[subQ1,subQ3]});Q71=makeQuery(id+"F0.imprint","IMPRINT",FACE,{"disambiguationData":[TD([[makeQuery(id+"F0.imprint","IMPRINT",EDGE,{"disambiguationData":[TD([[subQ4,-1.0]])],"derivedFrom":subQ1}),-1.0]])]});}
            var Q72;
            {var subQ1=sQuery(id+"F0.wireOp",EDGE,"E16.2.2");var subQ3=sQuery(id+"F0.wireOp",EDGE,"E41");var subQ4=makeQuery(id+"F0.imprint","INTERSECT",VERTEX,{"derivedFrom":[subQ1,subQ3]});Q72=makeQuery(id+"F0.imprint","IMPRINT",FACE,{"disambiguationData":[TD([[makeQuery(id+"F0.imprint","IMPRINT",EDGE,{"disambiguationData":[TD([[subQ4,1.0]])],"derivedFrom":subQ1}),-1.0]])]});}
            var Q73;
            {var subQ1=sQuery(id+"F0.wireOp",EDGE,"E15.bottom");var subQ3=sQuery(id+"F0.wireOp",EDGE,"E41");var subQ4=makeQuery(id+"F0.imprint","INTERSECT",VERTEX,{"derivedFrom":[subQ1,subQ3]});Q73=makeQuery(id+"F0.imprint","IMPRINT",FACE,{"disambiguationData":[TD([[makeQuery(id+"F0.imprint","IMPRINT",EDGE,{"disambiguationData":[TD([[subQ4,1.0]])],"derivedFrom":subQ1}),-1.0]])]});}
            var Q74;
            {var subQ1=sQuery(id+"F0.wireOp",EDGE,"E15.right");var subQ3=sQuery(id+"F0.wireOp",EDGE,"E41");var subQ4=makeQuery(id+"F0.imprint","INTERSECT",VERTEX,{"derivedFrom":[subQ1,subQ3]});Q74=makeQuery(id+"F0.imprint","IMPRINT",FACE,{"disambiguationData":[TD([[makeQuery(id+"F0.imprint","IMPRINT",EDGE,{"disambiguationData":[TD([[subQ4,-1.0]])],"derivedFrom":subQ1}),-1.0]])]});}
            var Q75;
            {var subQ1=sQuery(id+"F0.wireOp",EDGE,"E16.1.2");var subQ3=sQuery(id+"F0.wireOp",EDGE,"E41");var subQ4=makeQuery(id+"F0.imprint","INTERSECT",VERTEX,{"derivedFrom":[subQ1,subQ3]});Q75=makeQuery(id+"F0.imprint","IMPRINT",FACE,{"disambiguationData":[TD([[makeQuery(id+"F0.imprint","IMPRINT",EDGE,{"disambiguationData":[TD([[subQ4,1.0]])],"derivedFrom":subQ1}),-1.0]])]});}
            var Q76;
            {var subQ1=sQuery(id+"F0.wireOp",EDGE,"E16.1.3");var subQ3=sQuery(id+"F0.wireOp",EDGE,"E41");var subQ4=makeQuery(id+"F0.imprint","INTERSECT",VERTEX,{"derivedFrom":[subQ1,subQ3]});Q76=makeQuery(id+"F0.imprint","IMPRINT",FACE,{"disambiguationData":[TD([[makeQuery(id+"F0.imprint","IMPRINT",EDGE,{"disambiguationData":[TD([[subQ4,-1.0]])],"derivedFrom":subQ1}),-1.0]])]});}
            var Q77;
            {var subQ1=sQuery(id+"F0.wireOp",EDGE,"E3");var subQ3=sQuery(id+"F0.wireOp",EDGE,"E43");var subQ4=makeQuery(id+"F0.imprint","INTERSECT",VERTEX,{"derivedFrom":[subQ1,subQ3]});Q77=makeQuery(id+"F0.imprint","IMPRINT",FACE,{"disambiguationData":[TD([[makeQuery(id+"F0.imprint","IMPRINT",EDGE,{"disambiguationData":[TD([[subQ4,1.0]])],"derivedFrom":subQ3}),1.0]])]});}
            var Q78;
            {var subQ1=sQuery(id+"F0.wireOp",EDGE,"E5");var subQ3=sQuery(id+"F0.wireOp",EDGE,"E43");var subQ4=makeQuery(id+"F0.imprint","INTERSECT",VERTEX,{"derivedFrom":[subQ1,subQ3]});Q78=makeQuery(id+"F0.imprint","IMPRINT",FACE,{"disambiguationData":[TD([[makeQuery(id+"F0.imprint","IMPRINT",EDGE,{"disambiguationData":[TD([[subQ4,-1.0]])],"derivedFrom":subQ3}),1.0]])]});}
            var Q79;
            {var subQ1=sQuery(id+"F0.wireOp",EDGE,"E4");var subQ3=sQuery(id+"F0.wireOp",EDGE,"E43");var subQ4=makeQuery(id+"F0.imprint","INTERSECT",VERTEX,{"derivedFrom":[subQ1,subQ3]});Q79=makeQuery(id+"F0.imprint","IMPRINT",FACE,{"disambiguationData":[TD([[makeQuery(id+"F0.imprint","IMPRINT",EDGE,{"disambiguationData":[TD([[subQ4,-1.0]])],"derivedFrom":subQ3}),1.0]])]});}
            var Q80;
            {var subQ1=sQuery(id+"F0.wireOp",EDGE,"E4");var subQ3=sQuery(id+"F0.wireOp",EDGE,"E43");var subQ4=makeQuery(id+"F0.imprint","INTERSECT",VERTEX,{"derivedFrom":[subQ1,subQ3]});Q80=makeQuery(id+"F0.imprint","IMPRINT",FACE,{"disambiguationData":[TD([[makeQuery(id+"F0.imprint","IMPRINT",EDGE,{"disambiguationData":[TD([[subQ4,1.0]])],"derivedFrom":subQ3}),1.0]])]});}
            var Q81;
            {var subQ1=sQuery(id+"F0.wireOp",EDGE,"E3");var subQ3=sQuery(id+"F0.wireOp",EDGE,"E43");var subQ4=makeQuery(id+"F0.imprint","INTERSECT",VERTEX,{"derivedFrom":[subQ1,subQ3]});Q81=makeQuery(id+"F0.imprint","IMPRINT",FACE,{"disambiguationData":[TD([[makeQuery(id+"F0.imprint","IMPRINT",EDGE,{"disambiguationData":[TD([[subQ4,-1.0]])],"derivedFrom":subQ3}),1.0]])]});}
            extrude(context, id + "F1", {"entities" : qUnion([Q0, Q1, Q2, Q3, Q4, Q5, Q6, Q7, Q8, Q9, Q10, Q11, Q12, Q13, Q14, Q15, Q16, Q17, Q18, Q19, Q20, Q21, Q22, Q23, Q24, Q25, Q26, Q27, Q28, Q29, Q30, Q31, Q32, Q33, Q34, Q35, Q36, Q37, Q38, Q39, Q40, Q41, Q42, Q43, Q44, Q45, Q46, Q47, Q48, Q49, Q50, Q51, Q52, Q53, Q54, Q55, Q56, Q57, Q58, Q59, Q60, Q61, Q62, Q63, Q64, Q65, Q66, Q67, Q68, Q69, Q70, Q71, Q72, Q73, Q74, Q75, Q76, Q77, Q78, Q79, Q80, Q81]), "depth" : 1 * mm, "offsetDistance" : 25 * mm});
        }
        {
            var Q0;
            Q0 = qSketchRegion(id + "F0", true);
            extrude(context, id + "F2", {"entities" : qUnion([Q0]), "operationType" : NewBodyOperationType.ADD, "depth" : 20 * mm, "offsetDistance" : 25 * mm});
        }
        {
            var Q0;
            {var subQ1=sQuery(id+"F0.wireOp",EDGE,"E4");var subQ3=sQuery(id+"F0.wireOp",EDGE,"E17");var subQ4=makeQuery(id+"F0.imprint","INTERSECT",VERTEX,{"derivedFrom":[subQ1,subQ3]});Q0=makeQuery(id+"F0.imprint","IMPRINT",FACE,{"disambiguationData":[TD([[makeQuery(id+"F0.imprint","IMPRINT",EDGE,{"disambiguationData":[TD([[subQ4,-1.0]])],"derivedFrom":subQ3}),1.0]])]});}
            var Q1;
            {var subQ1=sQuery(id+"F0.wireOp",EDGE,"E5");var subQ3=sQuery(id+"F0.wireOp",EDGE,"E17");var subQ4=makeQuery(id+"F0.imprint","INTERSECT",VERTEX,{"derivedFrom":[subQ1,subQ3]});Q1=makeQuery(id+"F0.imprint","IMPRINT",FACE,{"disambiguationData":[TD([[makeQuery(id+"F0.imprint","IMPRINT",EDGE,{"disambiguationData":[TD([[subQ4,-1.0]])],"derivedFrom":subQ3}),1.0]])]});}
            var Q2;
            {var subQ1=sQuery(id+"F0.wireOp",EDGE,"E3");var subQ3=sQuery(id+"F0.wireOp",EDGE,"E17");var subQ4=makeQuery(id+"F0.imprint","INTERSECT",VERTEX,{"derivedFrom":[subQ1,subQ3]});Q2=makeQuery(id+"F0.imprint","IMPRINT",FACE,{"disambiguationData":[TD([[makeQuery(id+"F0.imprint","IMPRINT",EDGE,{"disambiguationData":[TD([[subQ4,1.0]])],"derivedFrom":subQ3}),1.0]])]});}
            var Q3;
            {var subQ1=sQuery(id+"F0.wireOp",EDGE,"E3");var subQ3=sQuery(id+"F0.wireOp",EDGE,"E17");var subQ4=makeQuery(id+"F0.imprint","INTERSECT",VERTEX,{"derivedFrom":[subQ1,subQ3]});Q3=makeQuery(id+"F0.imprint","IMPRINT",FACE,{"disambiguationData":[TD([[makeQuery(id+"F0.imprint","IMPRINT",EDGE,{"disambiguationData":[TD([[subQ4,-1.0]])],"derivedFrom":subQ3}),1.0]])]});}
            var Q4;
            {var subQ1=sQuery(id+"F0.wireOp",EDGE,"E4");var subQ3=sQuery(id+"F0.wireOp",EDGE,"E17");var subQ4=makeQuery(id+"F0.imprint","INTERSECT",VERTEX,{"derivedFrom":[subQ1,subQ3]});Q4=makeQuery(id+"F0.imprint","IMPRINT",FACE,{"disambiguationData":[TD([[makeQuery(id+"F0.imprint","IMPRINT",EDGE,{"disambiguationData":[TD([[subQ4,1.0]])],"derivedFrom":subQ3}),1.0]])]});}
            extrude(context, id + "F3", {"entities" : qUnion([Q0, Q1, Q2, Q3, Q4]), "operationType" : NewBodyOperationType.ADD, "depth" : 10 * mm, "offsetDistance" : 25 * mm});
        }
        {
            var Q0;
            {var subQ0=sQuery(id+"F0.wireOp",EDGE,"E10.top");Q0=makeQuery(id+"F0.imprint","IMPRINT",FACE,{"disambiguationData":[TD([[makeQuery(id+"F0.imprint","IMPRINT",EDGE,{"derivedFrom":subQ0}),-1.0]])]});}
            var Q1;
            {var subQ0=sQuery(id+"F0.wireOp",EDGE,"E10.left");Q1=makeQuery(id+"F0.imprint","IMPRINT",FACE,{"disambiguationData":[TD([[makeQuery(id+"F0.imprint","IMPRINT",EDGE,{"derivedFrom":subQ0}),-1.0]])]});}
            var Q2;
            {var subQ1=sQuery(id+"F0.wireOp",EDGE,"E4");var subQ3=sQuery(id+"F0.wireOp",EDGE,"E10.bottom");var subQ4=makeQuery(id+"F0.imprint","INTERSECT",VERTEX,{"derivedFrom":[subQ1,subQ3]});Q2=makeQuery(id+"F0.imprint","IMPRINT",FACE,{"disambiguationData":[TD([[makeQuery(id+"F0.imprint","IMPRINT",EDGE,{"disambiguationData":[TD([[subQ4,1.0]])],"derivedFrom":subQ1}),-1.0]])]});}
            var Q3;
            {var subQ1=sQuery(id+"F0.wireOp",EDGE,"E4");var subQ3=sQuery(id+"F0.wireOp",EDGE,"E10.bottom");var subQ4=makeQuery(id+"F0.imprint","INTERSECT",VERTEX,{"derivedFrom":[subQ1,subQ3]});Q3=makeQuery(id+"F0.imprint","IMPRINT",FACE,{"disambiguationData":[TD([[makeQuery(id+"F0.imprint","IMPRINT",EDGE,{"disambiguationData":[TD([[subQ4,1.0]])],"derivedFrom":subQ1}),1.0]])]});}
            var Q4;
            {var subQ0=sQuery(id+"F0.wireOp",EDGE,"E10.right");Q4=makeQuery(id+"F0.imprint","IMPRINT",FACE,{"disambiguationData":[TD([[makeQuery(id+"F0.imprint","IMPRINT",EDGE,{"derivedFrom":subQ0}),1.0]])]});}
            var Q5;
            {var subQ0=sQuery(id+"F0.wireOp",EDGE,"E13.3.2");Q5=makeQuery(id+"F0.imprint","IMPRINT",FACE,{"disambiguationData":[TD([[makeQuery(id+"F0.imprint","IMPRINT",EDGE,{"derivedFrom":subQ0}),-1.0]])]});}
            var Q6;
            {var subQ0=sQuery(id+"F0.wireOp",EDGE,"E13.3.1");Q6=makeQuery(id+"F0.imprint","IMPRINT",FACE,{"disambiguationData":[TD([[makeQuery(id+"F0.imprint","IMPRINT",EDGE,{"derivedFrom":subQ0}),1.0]])]});}
            var Q7;
            {var subQ0=sQuery(id+"F0.wireOp",EDGE,"E13.3.0");Q7=makeQuery(id+"F0.imprint","IMPRINT",FACE,{"disambiguationData":[TD([[makeQuery(id+"F0.imprint","IMPRINT",EDGE,{"derivedFrom":subQ0}),1.0]])]});}
            var Q8;
            {var subQ0=sQuery(id+"F0.wireOp",EDGE,"E13.3.3");Q8=makeQuery(id+"F0.imprint","IMPRINT",FACE,{"disambiguationData":[TD([[makeQuery(id+"F0.imprint","IMPRINT",EDGE,{"derivedFrom":subQ0}),-1.0]])]});}
            var Q9;
            {var subQ0=sQuery(id+"F0.wireOp",EDGE,"E16.3.1");Q9=makeQuery(id+"F0.imprint","IMPRINT",FACE,{"disambiguationData":[TD([[makeQuery(id+"F0.imprint","IMPRINT",EDGE,{"derivedFrom":subQ0}),1.0]])]});}
            var Q10;
            {var subQ1=sQuery(id+"F0.wireOp",EDGE,"E16.3.2");var subQ3=sQuery(id+"F0.wireOp",EDGE,"E41");var subQ4=makeQuery(id+"F0.imprint","INTERSECT",VERTEX,{"derivedFrom":[subQ1,subQ3]});Q10=makeQuery(id+"F0.imprint","IMPRINT",FACE,{"disambiguationData":[TD([[makeQuery(id+"F0.imprint","IMPRINT",EDGE,{"disambiguationData":[TD([[subQ4,-1.0]])],"derivedFrom":subQ1}),-1.0]])]});}
            var Q11;
            {var subQ0=sQuery(id+"F0.wireOp",EDGE,"E16.3.0");Q11=makeQuery(id+"F0.imprint","IMPRINT",FACE,{"disambiguationData":[TD([[makeQuery(id+"F0.imprint","IMPRINT",EDGE,{"derivedFrom":subQ0}),1.0]])]});}
            var Q12;
            {var subQ1=sQuery(id+"F0.wireOp",EDGE,"E16.3.3");var subQ3=sQuery(id+"F0.wireOp",EDGE,"E41");var subQ4=makeQuery(id+"F0.imprint","INTERSECT",VERTEX,{"derivedFrom":[subQ1,subQ3]});Q12=makeQuery(id+"F0.imprint","IMPRINT",FACE,{"disambiguationData":[TD([[makeQuery(id+"F0.imprint","IMPRINT",EDGE,{"disambiguationData":[TD([[subQ4,1.0]])],"derivedFrom":subQ1}),-1.0]])]});}
            var Q13;
            {var subQ1=sQuery(id+"F0.wireOp",EDGE,"E16.3.3");var subQ3=sQuery(id+"F0.wireOp",EDGE,"E41");var subQ4=makeQuery(id+"F0.imprint","INTERSECT",VERTEX,{"derivedFrom":[subQ1,subQ3]});Q13=makeQuery(id+"F0.imprint","IMPRINT",FACE,{"disambiguationData":[TD([[makeQuery(id+"F0.imprint","IMPRINT",EDGE,{"disambiguationData":[TD([[subQ4,-1.0]])],"derivedFrom":subQ1}),-1.0]])]});}
            var Q14;
            {var subQ1=sQuery(id+"F0.wireOp",EDGE,"E16.3.2");var subQ3=sQuery(id+"F0.wireOp",EDGE,"E41");var subQ4=makeQuery(id+"F0.imprint","INTERSECT",VERTEX,{"derivedFrom":[subQ1,subQ3]});Q14=makeQuery(id+"F0.imprint","IMPRINT",FACE,{"disambiguationData":[TD([[makeQuery(id+"F0.imprint","IMPRINT",EDGE,{"disambiguationData":[TD([[subQ4,1.0]])],"derivedFrom":subQ1}),-1.0]])]});}
            var Q15;
            {var subQ0=sQuery(id+"F0.wireOp",EDGE,"E16.2.0");Q15=makeQuery(id+"F0.imprint","IMPRINT",FACE,{"disambiguationData":[TD([[makeQuery(id+"F0.imprint","IMPRINT",EDGE,{"derivedFrom":subQ0}),1.0]])]});}
            var Q16;
            {var subQ1=sQuery(id+"F0.wireOp",EDGE,"E16.2.3");var subQ3=sQuery(id+"F0.wireOp",EDGE,"E41");var subQ4=makeQuery(id+"F0.imprint","INTERSECT",VERTEX,{"derivedFrom":[subQ1,subQ3]});Q16=makeQuery(id+"F0.imprint","IMPRINT",FACE,{"disambiguationData":[TD([[makeQuery(id+"F0.imprint","IMPRINT",EDGE,{"disambiguationData":[TD([[subQ4,1.0]])],"derivedFrom":subQ1}),-1.0]])]});}
            var Q17;
            {var subQ1=sQuery(id+"F0.wireOp",EDGE,"E16.2.2");var subQ3=sQuery(id+"F0.wireOp",EDGE,"E41");var subQ4=makeQuery(id+"F0.imprint","INTERSECT",VERTEX,{"derivedFrom":[subQ1,subQ3]});Q17=makeQuery(id+"F0.imprint","IMPRINT",FACE,{"disambiguationData":[TD([[makeQuery(id+"F0.imprint","IMPRINT",EDGE,{"disambiguationData":[TD([[subQ4,-1.0]])],"derivedFrom":subQ1}),-1.0]])]});}
            var Q18;
            {var subQ0=sQuery(id+"F0.wireOp",EDGE,"E16.2.1");Q18=makeQuery(id+"F0.imprint","IMPRINT",FACE,{"disambiguationData":[TD([[makeQuery(id+"F0.imprint","IMPRINT",EDGE,{"derivedFrom":subQ0}),1.0]])]});}
            var Q19;
            {var subQ1=sQuery(id+"F0.wireOp",EDGE,"E16.2.3");var subQ3=sQuery(id+"F0.wireOp",EDGE,"E41");var subQ4=makeQuery(id+"F0.imprint","INTERSECT",VERTEX,{"derivedFrom":[subQ1,subQ3]});Q19=makeQuery(id+"F0.imprint","IMPRINT",FACE,{"disambiguationData":[TD([[makeQuery(id+"F0.imprint","IMPRINT",EDGE,{"disambiguationData":[TD([[subQ4,-1.0]])],"derivedFrom":subQ1}),-1.0]])]});}
            var Q20;
            {var subQ1=sQuery(id+"F0.wireOp",EDGE,"E16.2.2");var subQ3=sQuery(id+"F0.wireOp",EDGE,"E41");var subQ4=makeQuery(id+"F0.imprint","INTERSECT",VERTEX,{"derivedFrom":[subQ1,subQ3]});Q20=makeQuery(id+"F0.imprint","IMPRINT",FACE,{"disambiguationData":[TD([[makeQuery(id+"F0.imprint","IMPRINT",EDGE,{"disambiguationData":[TD([[subQ4,1.0]])],"derivedFrom":subQ1}),-1.0]])]});}
            var Q21;
            {var subQ0=sQuery(id+"F0.wireOp",EDGE,"E13.2.3");Q21=makeQuery(id+"F0.imprint","IMPRINT",FACE,{"disambiguationData":[TD([[makeQuery(id+"F0.imprint","IMPRINT",EDGE,{"derivedFrom":subQ0}),-1.0]])]});}
            var Q22;
            {var subQ0=sQuery(id+"F0.wireOp",EDGE,"E13.2.0");Q22=makeQuery(id+"F0.imprint","IMPRINT",FACE,{"disambiguationData":[TD([[makeQuery(id+"F0.imprint","IMPRINT",EDGE,{"derivedFrom":subQ0}),1.0]])]});}
            var Q23;
            {var subQ0=sQuery(id+"F0.wireOp",EDGE,"E13.2.1");Q23=makeQuery(id+"F0.imprint","IMPRINT",FACE,{"disambiguationData":[TD([[makeQuery(id+"F0.imprint","IMPRINT",EDGE,{"derivedFrom":subQ0}),1.0]])]});}
            var Q24;
            {var subQ0=sQuery(id+"F0.wireOp",EDGE,"E13.2.2");Q24=makeQuery(id+"F0.imprint","IMPRINT",FACE,{"disambiguationData":[TD([[makeQuery(id+"F0.imprint","IMPRINT",EDGE,{"derivedFrom":subQ0}),-1.0]])]});}
            var Q25;
            {var subQ0=sQuery(id+"F0.wireOp",EDGE,"E7.bottom");Q25=makeQuery(id+"F0.imprint","IMPRINT",FACE,{"disambiguationData":[TD([[makeQuery(id+"F0.imprint","IMPRINT",EDGE,{"derivedFrom":subQ0}),-1.0]])]});}
            var Q26;
            {var subQ1=sQuery(id+"F0.wireOp",EDGE,"E6");var subQ3=sQuery(id+"F0.wireOp",EDGE,"E7.left");var subQ4=makeQuery(id+"F0.imprint","INTERSECT",VERTEX,{"derivedFrom":[subQ1,subQ3]});Q26=makeQuery(id+"F0.imprint","IMPRINT",FACE,{"disambiguationData":[TD([[makeQuery(id+"F0.imprint","IMPRINT",EDGE,{"disambiguationData":[TD([[subQ4,-1.0]])],"derivedFrom":subQ1}),1.0]])]});}
            var Q27;
            {var subQ1=sQuery(id+"F0.wireOp",EDGE,"E6");var subQ3=sQuery(id+"F0.wireOp",EDGE,"E7.left");var subQ4=makeQuery(id+"F0.imprint","INTERSECT",VERTEX,{"derivedFrom":[subQ1,subQ3]});Q27=makeQuery(id+"F0.imprint","IMPRINT",FACE,{"disambiguationData":[TD([[makeQuery(id+"F0.imprint","IMPRINT",EDGE,{"disambiguationData":[TD([[subQ4,-1.0]])],"derivedFrom":subQ1}),-1.0]])]});}
            var Q28;
            {var subQ0=sQuery(id+"F0.wireOp",EDGE,"E7.top");Q28=makeQuery(id+"F0.imprint","IMPRINT",FACE,{"disambiguationData":[TD([[makeQuery(id+"F0.imprint","IMPRINT",EDGE,{"derivedFrom":subQ0}),1.0]])]});}
            var Q29;
            {var subQ0=sQuery(id+"F0.wireOp",EDGE,"E7.right");Q29=makeQuery(id+"F0.imprint","IMPRINT",FACE,{"disambiguationData":[TD([[makeQuery(id+"F0.imprint","IMPRINT",EDGE,{"derivedFrom":subQ0}),-1.0]])]});}
            var Q30;
            {var subQ0=sQuery(id+"F0.wireOp",EDGE,"E9.bottom");Q30=makeQuery(id+"F0.imprint","IMPRINT",FACE,{"disambiguationData":[TD([[makeQuery(id+"F0.imprint","IMPRINT",EDGE,{"derivedFrom":subQ0}),-1.0]])]});}
            var Q31;
            {var subQ0=sQuery(id+"F0.wireOp",EDGE,"E9.left");Q31=makeQuery(id+"F0.imprint","IMPRINT",FACE,{"disambiguationData":[TD([[makeQuery(id+"F0.imprint","IMPRINT",EDGE,{"derivedFrom":subQ0}),1.0]])]});}
            var Q32;
            {var subQ1=sQuery(id+"F0.wireOp",EDGE,"E5");var subQ3=sQuery(id+"F0.wireOp",EDGE,"E9.right");var subQ4=makeQuery(id+"F0.imprint","INTERSECT",VERTEX,{"derivedFrom":[subQ1,subQ3]});Q32=makeQuery(id+"F0.imprint","IMPRINT",FACE,{"disambiguationData":[TD([[makeQuery(id+"F0.imprint","IMPRINT",EDGE,{"disambiguationData":[TD([[subQ4,-1.0]])],"derivedFrom":subQ1}),-1.0]])]});}
            var Q33;
            {var subQ1=sQuery(id+"F0.wireOp",EDGE,"E5");var subQ3=sQuery(id+"F0.wireOp",EDGE,"E9.right");var subQ4=makeQuery(id+"F0.imprint","INTERSECT",VERTEX,{"derivedFrom":[subQ1,subQ3]});Q33=makeQuery(id+"F0.imprint","IMPRINT",FACE,{"disambiguationData":[TD([[makeQuery(id+"F0.imprint","IMPRINT",EDGE,{"disambiguationData":[TD([[subQ4,-1.0]])],"derivedFrom":subQ1}),1.0]])]});}
            var Q34;
            {var subQ0=sQuery(id+"F0.wireOp",EDGE,"E9.top");Q34=makeQuery(id+"F0.imprint","IMPRINT",FACE,{"disambiguationData":[TD([[makeQuery(id+"F0.imprint","IMPRINT",EDGE,{"derivedFrom":subQ0}),1.0]])]});}
            var Q35;
            {var subQ0=sQuery(id+"F0.wireOp",EDGE,"E15.right");var subQ3=sQuery(id+"F0.wireOp",EDGE,"E41");var subQ5=makeQuery(id+"F0.imprint","INTERSECT",VERTEX,{"derivedFrom":[subQ0,subQ3]});Q35=makeQuery(id+"F0.imprint","IMPRINT",FACE,{"disambiguationData":[TD([[makeQuery(id+"F0.imprint","IMPRINT",EDGE,{"disambiguationData":[TD([[subQ5,1.0]])],"derivedFrom":subQ0}),-1.0]])]});}
            var Q36;
            {var subQ0=sQuery(id+"F0.wireOp",EDGE,"E15.left");Q36=makeQuery(id+"F0.imprint","IMPRINT",FACE,{"disambiguationData":[TD([[makeQuery(id+"F0.imprint","IMPRINT",EDGE,{"derivedFrom":subQ0}),1.0]])]});}
            var Q37;
            {var subQ0=sQuery(id+"F0.wireOp",EDGE,"E15.bottom");var subQ3=sQuery(id+"F0.wireOp",EDGE,"E41");var subQ5=makeQuery(id+"F0.imprint","INTERSECT",VERTEX,{"derivedFrom":[subQ0,subQ3]});Q37=makeQuery(id+"F0.imprint","IMPRINT",FACE,{"disambiguationData":[TD([[makeQuery(id+"F0.imprint","IMPRINT",EDGE,{"disambiguationData":[TD([[subQ5,-1.0]])],"derivedFrom":subQ0}),-1.0]])]});}
            var Q38;
            {var subQ0=sQuery(id+"F0.wireOp",EDGE,"E15.top");Q38=makeQuery(id+"F0.imprint","IMPRINT",FACE,{"disambiguationData":[TD([[makeQuery(id+"F0.imprint","IMPRINT",EDGE,{"derivedFrom":subQ0}),1.0]])]});}
            var Q39;
            {var subQ1=sQuery(id+"F0.wireOp",EDGE,"E15.bottom");var subQ3=sQuery(id+"F0.wireOp",EDGE,"E41");var subQ4=makeQuery(id+"F0.imprint","INTERSECT",VERTEX,{"derivedFrom":[subQ1,subQ3]});Q39=makeQuery(id+"F0.imprint","IMPRINT",FACE,{"disambiguationData":[TD([[makeQuery(id+"F0.imprint","IMPRINT",EDGE,{"disambiguationData":[TD([[subQ4,1.0]])],"derivedFrom":subQ1}),-1.0]])]});}
            var Q40;
            {var subQ1=sQuery(id+"F0.wireOp",EDGE,"E15.right");var subQ3=sQuery(id+"F0.wireOp",EDGE,"E41");var subQ4=makeQuery(id+"F0.imprint","INTERSECT",VERTEX,{"derivedFrom":[subQ1,subQ3]});Q40=makeQuery(id+"F0.imprint","IMPRINT",FACE,{"disambiguationData":[TD([[makeQuery(id+"F0.imprint","IMPRINT",EDGE,{"disambiguationData":[TD([[subQ4,-1.0]])],"derivedFrom":subQ1}),-1.0]])]});}
            var Q41;
            {var subQ1=sQuery(id+"F0.wireOp",EDGE,"E16.1.3");var subQ3=sQuery(id+"F0.wireOp",EDGE,"E41");var subQ4=makeQuery(id+"F0.imprint","INTERSECT",VERTEX,{"derivedFrom":[subQ1,subQ3]});Q41=makeQuery(id+"F0.imprint","IMPRINT",FACE,{"disambiguationData":[TD([[makeQuery(id+"F0.imprint","IMPRINT",EDGE,{"disambiguationData":[TD([[subQ4,1.0]])],"derivedFrom":subQ1}),-1.0]])]});}
            var Q42;
            {var subQ1=sQuery(id+"F0.wireOp",EDGE,"E16.1.3");var subQ3=sQuery(id+"F0.wireOp",EDGE,"E41");var subQ4=makeQuery(id+"F0.imprint","INTERSECT",VERTEX,{"derivedFrom":[subQ1,subQ3]});Q42=makeQuery(id+"F0.imprint","IMPRINT",FACE,{"disambiguationData":[TD([[makeQuery(id+"F0.imprint","IMPRINT",EDGE,{"disambiguationData":[TD([[subQ4,-1.0]])],"derivedFrom":subQ1}),-1.0]])]});}
            var Q43;
            {var subQ0=sQuery(id+"F0.wireOp",EDGE,"E16.1.0");Q43=makeQuery(id+"F0.imprint","IMPRINT",FACE,{"disambiguationData":[TD([[makeQuery(id+"F0.imprint","IMPRINT",EDGE,{"derivedFrom":subQ0}),1.0]])]});}
            var Q44;
            {var subQ1=sQuery(id+"F0.wireOp",EDGE,"E16.1.2");var subQ3=sQuery(id+"F0.wireOp",EDGE,"E41");var subQ4=makeQuery(id+"F0.imprint","INTERSECT",VERTEX,{"derivedFrom":[subQ1,subQ3]});Q44=makeQuery(id+"F0.imprint","IMPRINT",FACE,{"disambiguationData":[TD([[makeQuery(id+"F0.imprint","IMPRINT",EDGE,{"disambiguationData":[TD([[subQ4,-1.0]])],"derivedFrom":subQ1}),-1.0]])]});}
            var Q45;
            {var subQ0=sQuery(id+"F0.wireOp",EDGE,"E16.1.1");Q45=makeQuery(id+"F0.imprint","IMPRINT",FACE,{"disambiguationData":[TD([[makeQuery(id+"F0.imprint","IMPRINT",EDGE,{"derivedFrom":subQ0}),1.0]])]});}
            var Q46;
            {var subQ1=sQuery(id+"F0.wireOp",EDGE,"E16.1.2");var subQ3=sQuery(id+"F0.wireOp",EDGE,"E41");var subQ4=makeQuery(id+"F0.imprint","INTERSECT",VERTEX,{"derivedFrom":[subQ1,subQ3]});Q46=makeQuery(id+"F0.imprint","IMPRINT",FACE,{"disambiguationData":[TD([[makeQuery(id+"F0.imprint","IMPRINT",EDGE,{"disambiguationData":[TD([[subQ4,1.0]])],"derivedFrom":subQ1}),-1.0]])]});}
            var Q47;
            {var subQ3=sQuery(id+"F0.wireOp",EDGE,"E12.bottom");Q47=makeQuery(id+"F0.imprint","IMPRINT",FACE,{"disambiguationData":[TD([[makeQuery(id+"F0.imprint","IMPRINT",EDGE,{"derivedFrom":subQ3}),-1.0]])]});}
            var Q48;
            {var subQ0=sQuery(id+"F0.wireOp",EDGE,"E12.left");Q48=makeQuery(id+"F0.imprint","IMPRINT",FACE,{"disambiguationData":[TD([[makeQuery(id+"F0.imprint","IMPRINT",EDGE,{"derivedFrom":subQ0}),1.0]])]});}
            var Q49;
            {var subQ0=sQuery(id+"F0.wireOp",EDGE,"E12.top");Q49=makeQuery(id+"F0.imprint","IMPRINT",FACE,{"disambiguationData":[TD([[makeQuery(id+"F0.imprint","IMPRINT",EDGE,{"derivedFrom":subQ0}),1.0]])]});}
            var Q50;
            {var subQ3=sQuery(id+"F0.wireOp",EDGE,"E12.right");Q50=makeQuery(id+"F0.imprint","IMPRINT",FACE,{"disambiguationData":[TD([[makeQuery(id+"F0.imprint","IMPRINT",EDGE,{"derivedFrom":subQ3}),-1.0]])]});}
            var Q51;
            {var subQ0=sQuery(id+"F0.wireOp",EDGE,"E13.1.3");Q51=makeQuery(id+"F0.imprint","IMPRINT",FACE,{"disambiguationData":[TD([[makeQuery(id+"F0.imprint","IMPRINT",EDGE,{"derivedFrom":subQ0}),-1.0]])]});}
            var Q52;
            {var subQ0=sQuery(id+"F0.wireOp",EDGE,"E13.1.0");Q52=makeQuery(id+"F0.imprint","IMPRINT",FACE,{"disambiguationData":[TD([[makeQuery(id+"F0.imprint","IMPRINT",EDGE,{"derivedFrom":subQ0}),1.0]])]});}
            var Q53;
            {var subQ0=sQuery(id+"F0.wireOp",EDGE,"E13.1.2");Q53=makeQuery(id+"F0.imprint","IMPRINT",FACE,{"disambiguationData":[TD([[makeQuery(id+"F0.imprint","IMPRINT",EDGE,{"derivedFrom":subQ0}),-1.0]])]});}
            var Q54;
            {var subQ0=sQuery(id+"F0.wireOp",EDGE,"E13.1.1");Q54=makeQuery(id+"F0.imprint","IMPRINT",FACE,{"disambiguationData":[TD([[makeQuery(id+"F0.imprint","IMPRINT",EDGE,{"derivedFrom":subQ0}),1.0]])]});}
            var Q55;
            {var subQ0=sQuery(id+"F0.wireOp",EDGE,"E8.right");Q55=makeQuery(id+"F0.imprint","IMPRINT",FACE,{"disambiguationData":[TD([[makeQuery(id+"F0.imprint","IMPRINT",EDGE,{"derivedFrom":subQ0}),-1.0]])]});}
            var Q56;
            {var subQ0=sQuery(id+"F0.wireOp",EDGE,"E8.top");Q56=makeQuery(id+"F0.imprint","IMPRINT",FACE,{"disambiguationData":[TD([[makeQuery(id+"F0.imprint","IMPRINT",EDGE,{"derivedFrom":subQ0}),1.0]])]});}
            var Q57;
            {var subQ0=sQuery(id+"F0.wireOp",EDGE,"E8.left");Q57=makeQuery(id+"F0.imprint","IMPRINT",FACE,{"disambiguationData":[TD([[makeQuery(id+"F0.imprint","IMPRINT",EDGE,{"derivedFrom":subQ0}),1.0]])]});}
            var Q58;
            {var subQ1=sQuery(id+"F0.wireOp",EDGE,"E3");var subQ3=sQuery(id+"F0.wireOp",EDGE,"E8.bottom");var subQ4=makeQuery(id+"F0.imprint","INTERSECT",VERTEX,{"derivedFrom":[subQ1,subQ3]});Q58=makeQuery(id+"F0.imprint","IMPRINT",FACE,{"disambiguationData":[TD([[makeQuery(id+"F0.imprint","IMPRINT",EDGE,{"disambiguationData":[TD([[subQ4,1.0]])],"derivedFrom":subQ1}),-1.0]])]});}
            var Q59;
            {var subQ1=sQuery(id+"F0.wireOp",EDGE,"E3");var subQ3=sQuery(id+"F0.wireOp",EDGE,"E8.bottom");var subQ4=makeQuery(id+"F0.imprint","INTERSECT",VERTEX,{"derivedFrom":[subQ1,subQ3]});Q59=makeQuery(id+"F0.imprint","IMPRINT",FACE,{"disambiguationData":[TD([[makeQuery(id+"F0.imprint","IMPRINT",EDGE,{"disambiguationData":[TD([[subQ4,1.0]])],"derivedFrom":subQ1}),1.0]])]});}
            extrude(context, id + "F4", {"entities" : qUnion([Q0, Q1, Q2, Q3, Q4, Q5, Q6, Q7, Q8, Q9, Q10, Q11, Q12, Q13, Q14, Q15, Q16, Q17, Q18, Q19, Q20, Q21, Q22, Q23, Q24, Q25, Q26, Q27, Q28, Q29, Q30, Q31, Q32, Q33, Q34, Q35, Q36, Q37, Q38, Q39, Q40, Q41, Q42, Q43, Q44, Q45, Q46, Q47, Q48, Q49, Q50, Q51, Q52, Q53, Q54, Q55, Q56, Q57, Q58, Q59]), "operationType" : NewBodyOperationType.ADD, "depth" : 15 * mm, "offsetDistance" : 25 * mm, "hasDraft" : true, "draftAngle" : 10 * degree, "draftPullDirection" : true});
        }
        {
            var Q0;
            Q0=makeQuery(id+"F2.opExtrude","CAP_EDGE",EDGE,{"disambiguationData":[OSD([sQuery(id+"F0.wireOp",EDGE,"E1")])],"isStart":false});
            fillet(context, id + "F5", {"entities" : qUnion([Q0]), "radius" : 1 * mm, "tangentPropagation" : true, "allowEdgeOverflow" : false});
        }
        {
            var Q0;
            Q0=makeQuery(id+"F3.boolean.opBoolean","SPLIT",FACE,{"disambiguationData":[TD([makeQuery(id+"F3.opExtrude","SWEPT_FACE",FACE,{"disambiguationData":[OSD([sQuery(id+"F0.wireOp",EDGE,"E43")])]})])],"derivedFrom":makeQuery(id+"F1.opExtrude","CAP_FACE",FACE,{"disambiguationData":[OSD([sQuery(id+"F0.wireOp",EDGE,"E1")])],"isStart":false})});
            extrude(context, id + "F6", {"entities" : qUnion([Q0]), "operationType" : NewBodyOperationType.ADD, "depth" : 5 * mm, "offsetDistance" : 25 * mm});
        }
    });
